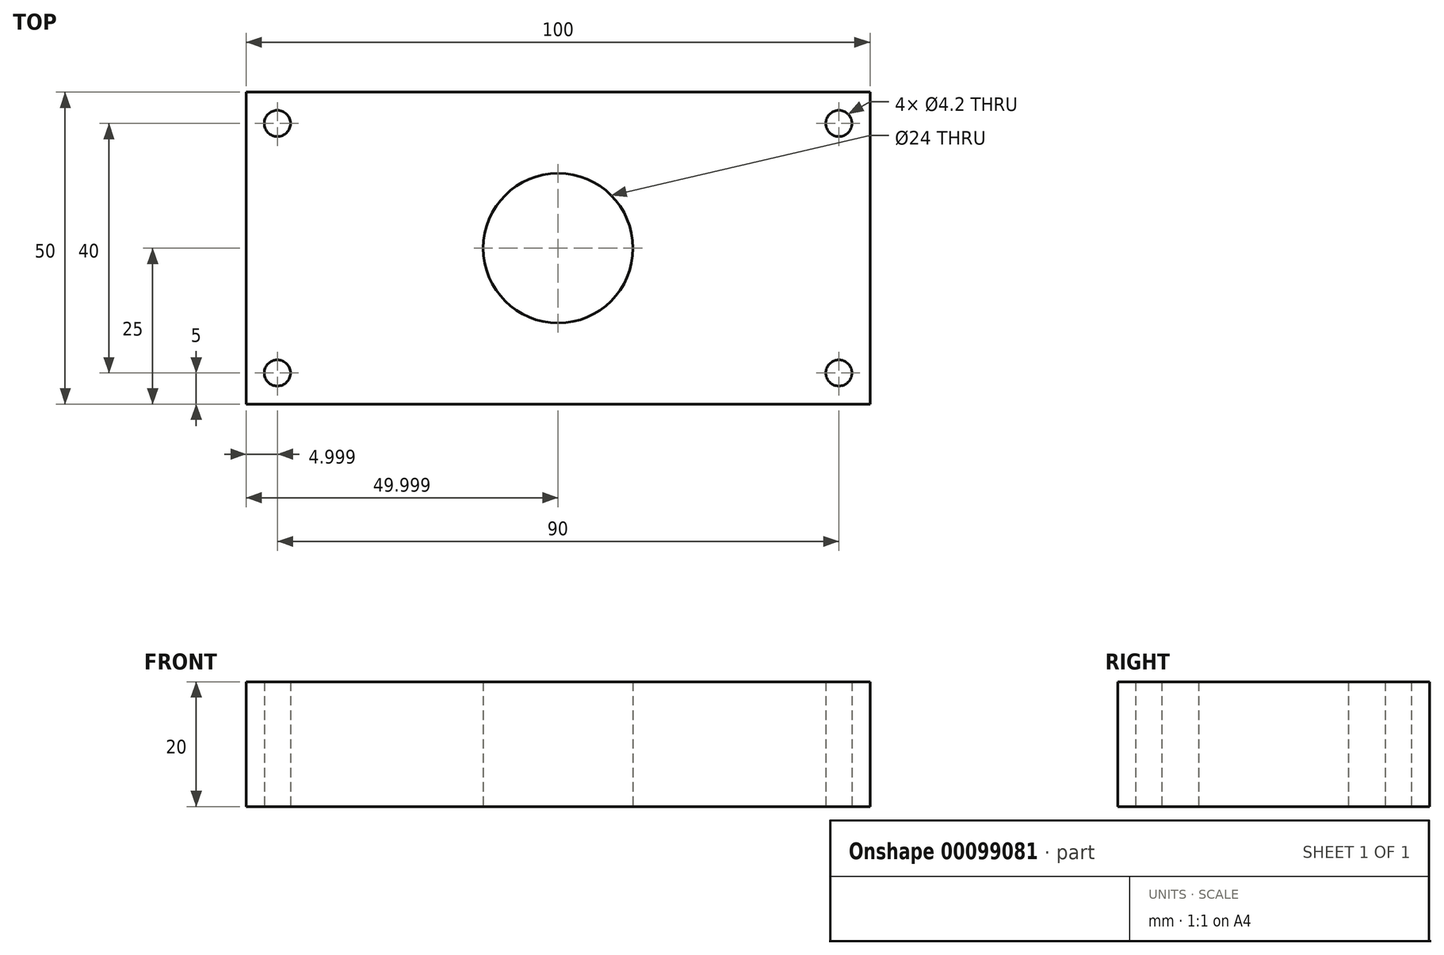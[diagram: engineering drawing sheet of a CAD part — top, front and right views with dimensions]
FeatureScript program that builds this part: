
annotation { "Feature Type Name" : "Feature", "Feature Type Description" : "" }
export const myFeature = defineFeature(function(context is Context, id is Id, definition is map)
    precondition{}
    {
        {
            var Q0;
            Q0=qCreatedBy(makeId("Top.planeOp"),FACE);
            var sketch = newSketch(context, id + "F0", { "sketchPlane" : qUnion([Q0])});
            skLineSegment(sketch, "E0.bottom", {"start": v(-32.07, 45) * mm, "end": v(67.93, 45) * mm});
            skLineSegment(sketch, "E0.top", {"start": v(-32.07, -5) * mm, "end": v(67.93, -5) * mm});
            skLineSegment(sketch, "E0.left", {"start": v(-32.07, 45) * mm, "end": v(-32.07, -5) * mm});
            skLineSegment(sketch, "E0.right", {"start": v(67.93, 45) * mm, "end": v(67.93, -5) * mm});
            skCircle(sketch, "E1", {"center": v(-27.07, 40) * mm, "radius": 2.1 * mm});
            skCircle(sketch, "E2", {"center": v(-27.07, 0) * mm, "radius": 2.1 * mm});
            skCircle(sketch, "E3", {"center": v(62.93, 40) * mm, "radius": 2.1 * mm});
            skCircle(sketch, "E4", {"center": v(62.93, 0) * mm, "radius": 2.1 * mm});
            skCircle(sketch, "E5", {"center": v(17.93, 20) * mm, "radius": 12 * mm});
            skSolve(sketch);
        }
        {
            var Q0;
            Q0=makeQuery(id+"F0.imprint","IMPRINT",FACE,{"disambiguationData":[TD([[makeQuery(id+"F0.imprint","IMPRINT",EDGE,{"derivedFrom":sQuery(id+"F0.wireOp",EDGE,"E0.bottom")}),-1.0]])]});
            extrude(context, id + "F1", {"entities" : qUnion([Q0]), "depth" : 20 * mm});
        }
    });
